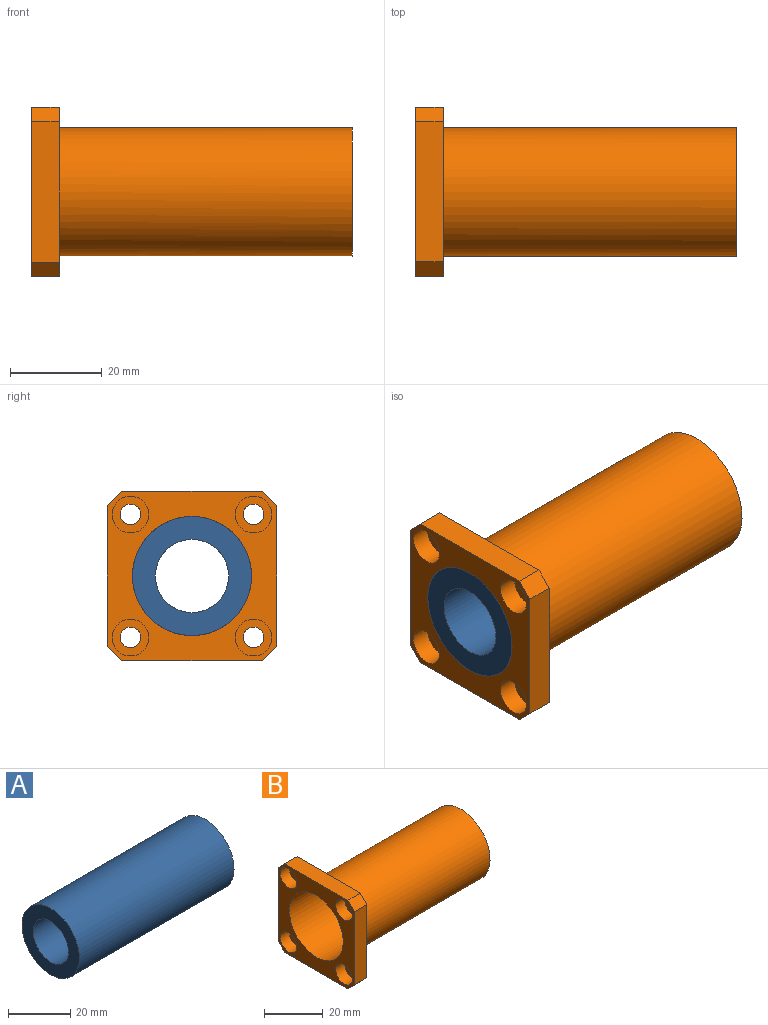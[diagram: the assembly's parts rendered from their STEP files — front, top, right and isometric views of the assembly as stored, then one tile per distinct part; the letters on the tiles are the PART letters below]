
ASSEMBLY  parts=2 mates=1
PART A: 4 faces, bbox 70x26x26 mm
  f0: plane 26x26mm, normal (1,0,0), area 329.9mm2, adj f2,f3
  f1: plane 26x26mm, normal (-1,0,0), area 329.9mm2, adj f2,f3
  f2: cylinder r=13mm len=70mm, axis (-1,0,0), area 5717.7mm2, adj f0,f1
  f3: cylinder r=8mm len=70mm, axis (-1,0,0), area 3518.6mm2, adj f0,f1
PART B: 25 faces, bbox 70x37x37 mm
  f0: cylinder r=2.25mm len=4.5mm, axis (-1,0,0), area 22.6mm2, adj f12,f19
  f1: cylinder r=2.25mm len=4.5mm, axis (-1,0,0), area 22.6mm2, adj f12,f17
  f2: cylinder r=2.25mm len=4.5mm, axis (-1,0,0), area 22.6mm2, adj f12,f15
  f3: cylinder r=2.25mm len=4.5mm, axis (-1,0,0), area 22.6mm2, adj f12,f21
  f4: plane 30.58x6mm, normal (0,0,-1), area 183.5mm2, adj f5,f11,f12,f13
  f5: plane 6x3.21mm, normal (0,0.71,-0.71), area 27.2mm2, adj f4,f6,f12,f13
  f6: plane 30.58x6mm, normal (0,1,0), area 183.5mm2, adj f5,f7,f12,f13
  f7: plane 6x3.21mm, normal (0,0.71,0.71), area 27.2mm2, adj f6,f8,f12,f13
  f8: plane 30.58x6mm, normal (0,0,1), area 183.5mm2, adj f7,f9,f12,f13
  f9: plane 6x3.21mm, normal (0,-0.71,0.71), area 27.2mm2, adj f8,f10,f12,f13
  f10: plane 30.58x6mm, normal (0,-1,0), area 183.5mm2, adj f9,f11,f12,f13
  f11: plane 6x3.21mm, normal (0,-0.71,-0.71), area 27.2mm2, adj f4,f10,f12,f13
  f12: plane 37x37mm, normal (1,0,0), area 669mm2, adj f0,f1,f2,f3,f4,f5,f6,f7
  f13: plane 37x37mm, normal (-1,0,0), area 616.4mm2, adj f4,f5,f6,f7,f8,f9,f10,f11
  f14: cylinder r=4mm len=8mm, axis (-1,0,0), area 110.6mm2, adj f13,f15
  f15: plane 8x8mm, normal (-1,0,0), area 34.4mm2, adj f2,f14
  f16: cylinder r=4mm len=8mm, axis (-1,0,0), area 110.6mm2, adj f13,f17
  f17: plane 8x8mm, normal (-1,0,0), area 34.4mm2, adj f1,f16
  f18: cylinder r=4mm len=8mm, axis (-1,0,0), area 110.6mm2, adj f13,f19
  f19: plane 8x8mm, normal (-1,0,0), area 34.4mm2, adj f0,f18
  f20: cylinder r=4mm len=8mm, axis (-1,0,0), area 110.6mm2, adj f13,f21
  f21: plane 8x8mm, normal (-1,0,0), area 34.4mm2, adj f3,f20
  f22: cylinder r=14mm len=64mm, axis (-1,0,0), area 5629.7mm2, adj f12,f23
  f23: plane 28x28mm, normal (1,0,0), area 84.8mm2, adj f22,f24
  f24: cylinder r=13mm len=70mm, axis (-1,0,0), area 5717.7mm2, adj f13,f23
PLACE A t=(-14.59,-1.18,-4.72)mm
PLACE B t=(-14.59,-1.18,-4.72)mm
MATE fastened A.f3 <-> B.f24  axis (-1,0,0) through (-14.59,-1.18,-4.72)mm
